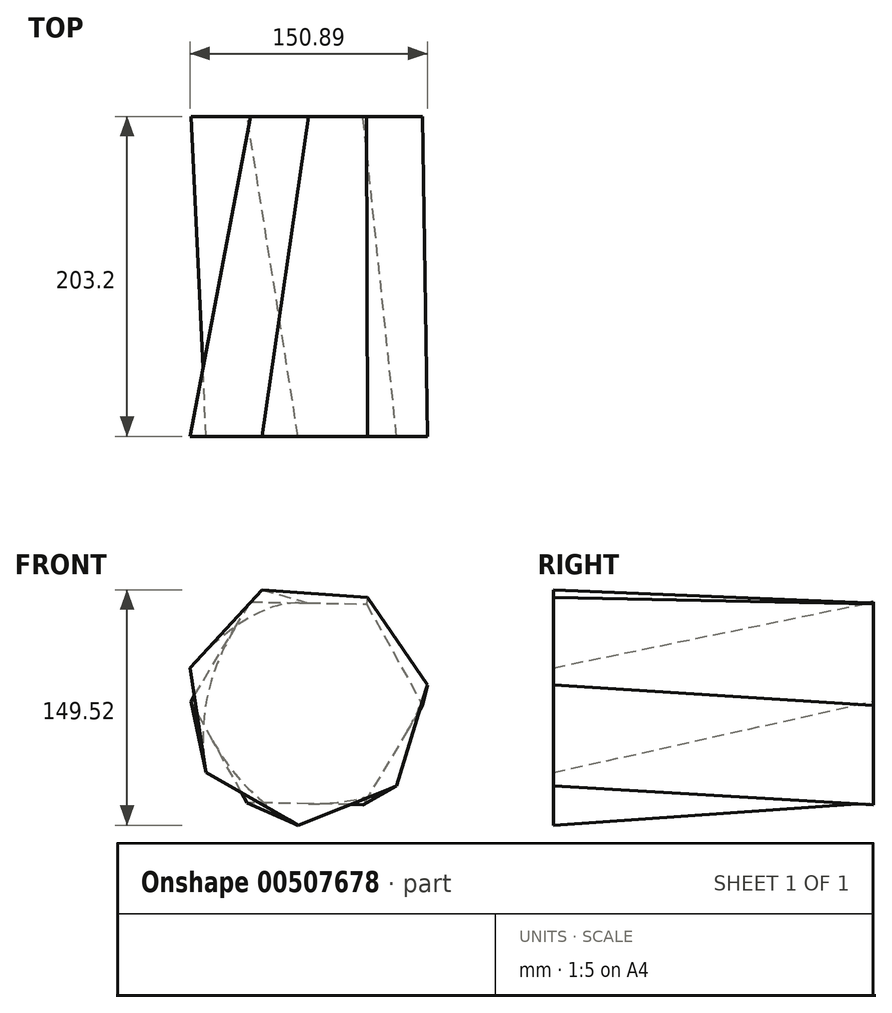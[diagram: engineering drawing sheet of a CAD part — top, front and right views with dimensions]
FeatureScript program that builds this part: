
annotation { "Feature Type Name" : "Feature", "Feature Type Description" : "" }
export const myFeature = defineFeature(function(context is Context, id is Id, definition is map)
    precondition{}
    {
        {
            var Q0;
            Q0=qCreatedBy(makeId("Front.planeOp"),FACE);
            var sketch = newSketch(context, id + "F0", { "sketchPlane" : qUnion([Q0])});
            skCircle(sketch, "E0.cCircle", {"center": v(0, 0) * mm, "radius": 73.6 * mm, "construction": true});
            skLineSegment(sketch, "E0.0", {"start": v(-37.9, -63.1) * mm, "end": v(-73.6, 1.26) * mm});
            skLineSegment(sketch, "E0.1", {"start": v(-73.6, 1.26) * mm, "end": v(-35.7, 64.37) * mm});
            skLineSegment(sketch, "E0.2", {"start": v(-35.7, 64.37) * mm, "end": v(37.9, 63.1) * mm});
            skLineSegment(sketch, "E0.3", {"start": v(37.9, 63.1) * mm, "end": v(73.6, -1.26) * mm});
            skLineSegment(sketch, "E0.4", {"start": v(73.6, -1.26) * mm, "end": v(35.7, -64.37) * mm});
            skLineSegment(sketch, "E0.5", {"start": v(35.7, -64.37) * mm, "end": v(-37.9, -63.1) * mm});
            skSolve(sketch);
        }
        {
            var Q0;
            Q0=qCreatedBy(makeId("Front.planeOp"),FACE);
            cPlane(context, id + "F1", {"entities" : qUnion([Q0]), "cplaneType" : CPlaneType.OFFSET, "offset" : 203.2 * mm, "width" : 152.4 * mm, "height" : 152.4 * mm});
        }
        {
            var Q0;
            Q0=qCreatedBy(id+"F1.planeOp",FACE);
            var sketch = newSketch(context, id + "F2", { "sketchPlane" : qUnion([Q0])});
            skCircle(sketch, "E1.cCircle", {"center": v(0, 0) * mm, "radius": 77.58 * mm, "construction": true});
            skLineSegment(sketch, "E1.0", {"start": v(-5.54, -77.39) * mm, "end": v(-63.96, -43.92) * mm});
            skLineSegment(sketch, "E1.1", {"start": v(-63.96, -43.92) * mm, "end": v(-74.21, 22.62) * mm});
            skLineSegment(sketch, "E1.2", {"start": v(-74.21, 22.62) * mm, "end": v(-28.59, 72.13) * mm});
            skLineSegment(sketch, "E1.3", {"start": v(-28.59, 72.13) * mm, "end": v(38.57, 67.32) * mm});
            skLineSegment(sketch, "E1.4", {"start": v(38.57, 67.32) * mm, "end": v(76.68, 11.82) * mm});
            skLineSegment(sketch, "E1.5", {"start": v(76.68, 11.82) * mm, "end": v(57.05, -52.58) * mm});
            skLineSegment(sketch, "E1.6", {"start": v(57.05, -52.58) * mm, "end": v(-5.54, -77.39) * mm});
            skSolve(sketch);
        }
        {
            var Q0;
            Q0=makeQuery(id+"F2.imprint","IMPRINT",FACE,{"disambiguationData":[TD([[makeQuery(id+"F2.imprint","IMPRINT",EDGE,{"derivedFrom":sQuery(id+"F2.wireOp",EDGE,"E1.0")}),-1.0]])]});
            var Q1;
            Q1=makeQuery(id+"F0.imprint","IMPRINT",FACE,{"disambiguationData":[TD([[makeQuery(id+"F0.imprint","IMPRINT",EDGE,{"derivedFrom":sQuery(id+"F0.wireOp",EDGE,"E0.0")}),-1.0]])]});
            loft(context, id + "F3", {"sheetProfilesArray" : [{ "sheetProfileEntities" : qUnion([Q0]) }, { "sheetProfileEntities" : qUnion([Q1]) }]});
        }
    });
